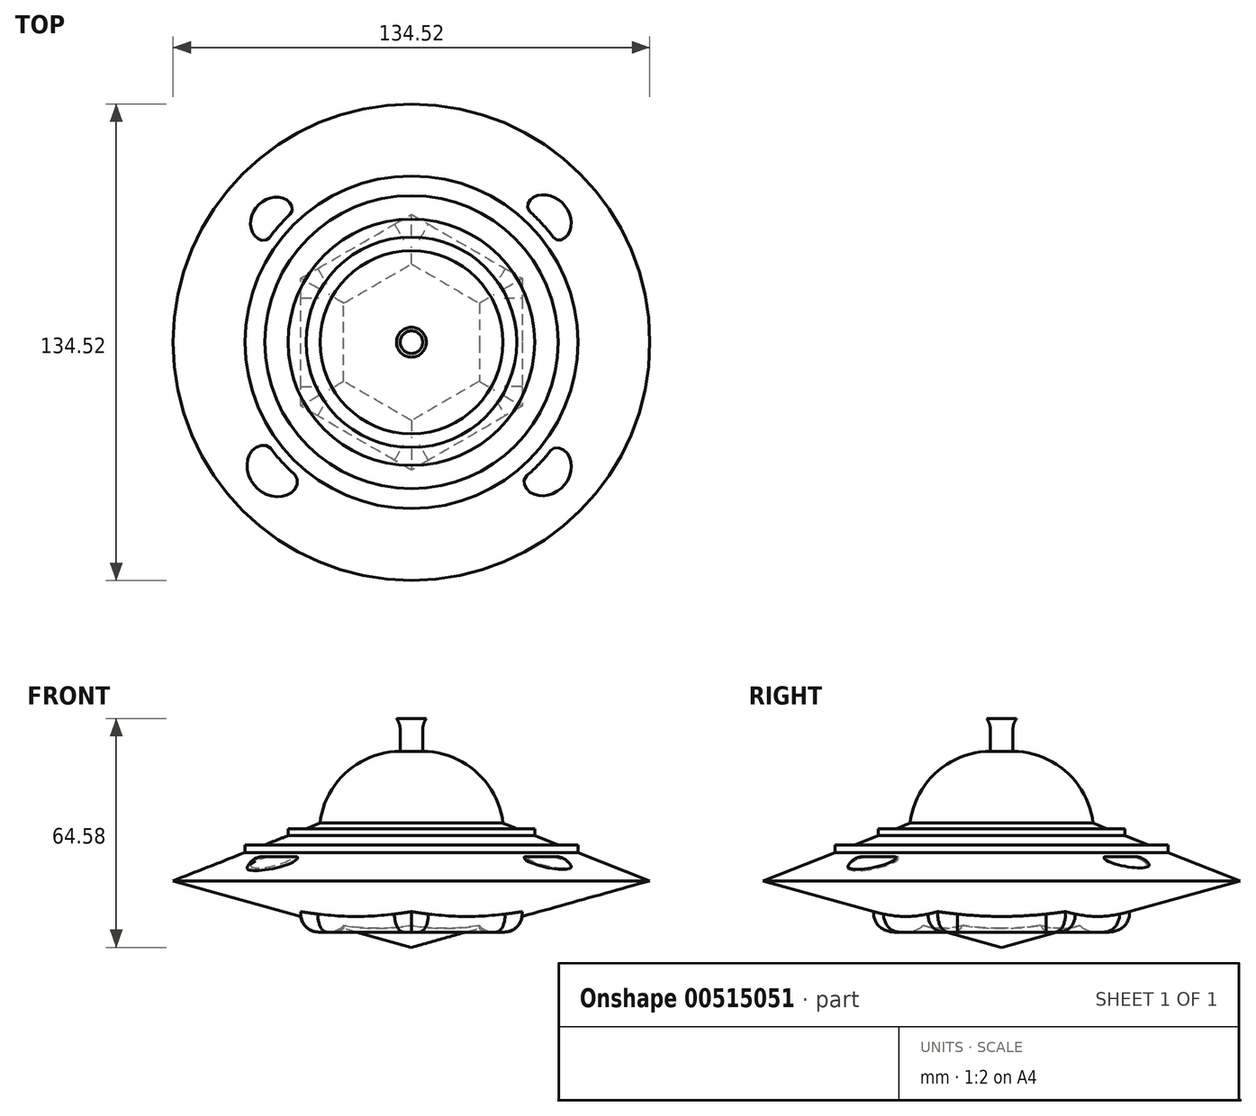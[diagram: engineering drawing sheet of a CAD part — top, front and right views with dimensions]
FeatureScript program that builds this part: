
annotation { "Feature Type Name" : "Feature", "Feature Type Description" : "" }
export const myFeature = defineFeature(function(context is Context, id is Id, definition is map)
    precondition{}
    {
        {
            var Q0;
            Q0=qCreatedBy(makeId("Front.planeOp"),FACE);
            var sketch = newSketch(context, id + "F0", { "sketchPlane" : qUnion([Q0])});
            skLineSegment(sketch, "E0", {"start": v(0, -18.8) * mm, "end": v(67.26, 0) * mm});
            skLineSegment(sketch, "E1", {"start": v(67.26, 0) * mm, "end": v(25.82, 16.26) * mm});
            skArc(sketch, "E2", {"start": v(25.82, 16.26) * mm, "mid": v(17.12, 31.7) * mm, "end": v(0, 36.34) * mm});
            skLineSegment(sketch, "E3", {"start": v(0, 36.34) * mm, "end": v(0, -18.8) * mm});
            skLineSegment(sketch, "E4", {"start": v(0, 36.34) * mm, "end": v(0, -18.8) * mm, "construction": true});
            skSolve(sketch);
        }
        {
            var Q0;
            Q0 = qSketchRegion(id + "F0", true);
            var Q1;
            Q1=sQuery(id+"F0.wireOp",EDGE,"E3");
            revolve(context, id + "F1", {"entities" : qUnion([Q0]), "axis" : qUnion([Q1]), "revolveType" : RevolveType.FULL});
        }
        {
            var Q0;
            Q0=qCreatedBy(makeId("Top.planeOp"),FACE);
            var sketch = newSketch(context, id + "F2", { "sketchPlane" : qUnion([Q0])});
            skCircle(sketch, "E5.cCircle", {"center": v(0, 0) * mm, "radius": 26.96 * mm, "construction": true});
            skLineSegment(sketch, "E5.0", {"start": v(31.13, 0.69) * mm, "end": v(16.16, -26.61) * mm});
            skLineSegment(sketch, "E5.1", {"start": v(16.16, -26.61) * mm, "end": v(-14.97, -27.3) * mm});
            skLineSegment(sketch, "E5.2", {"start": v(-14.97, -27.3) * mm, "end": v(-31.13, -0.69) * mm});
            skLineSegment(sketch, "E5.3", {"start": v(-31.13, -0.69) * mm, "end": v(-16.16, 26.61) * mm});
            skLineSegment(sketch, "E5.4", {"start": v(-16.16, 26.61) * mm, "end": v(14.97, 27.3) * mm});
            skLineSegment(sketch, "E5.5", {"start": v(14.97, 27.3) * mm, "end": v(31.13, 0.69) * mm});
            skPoint(sketch, "E5.0.midPoint", {"position": v(23.64, -12.96) * mm});
            skSolve(sketch);
        }
        {
            var Q0;
            Q0 = qSketchRegion(id + "F2", true);
            extrude(context, id + "F3", {"entities" : qUnion([Q0]), "operationType" : NewBodyOperationType.ADD, "oppositeDirection" : true, "depth" : 5.33 * mm, "offsetDistance" : 25.4 * mm});
        }
        {
            var Q0;
            Q0=qCreatedBy(makeId("Top.planeOp"),FACE);
            var sketch = newSketch(context, id + "F4", { "sketchPlane" : qUnion([Q0])});
            skCircle(sketch, "E6", {"center": v(-36.65, 32.37) * mm, "radius": 9.48 * mm});
            skCircle(sketch, "E7", {"center": v(35.69, 32.37) * mm, "radius": 10.16 * mm});
            skCircle(sketch, "E8", {"center": v(35.69, -33.96) * mm, "radius": 9.99 * mm});
            skCircle(sketch, "E9", {"center": v(-36.65, -33.96) * mm, "radius": 10.14 * mm});
            skSolve(sketch);
        }
        {
            var Q0;
            Q0 = qSketchRegion(id + "F4", true);
            extrude(context, id + "F5", {"entities" : qUnion([Q0]), "operationType" : NewBodyOperationType.ADD, "depth" : 6.86 * mm, "offsetDistance" : 25.4 * mm});
        }
        {
            var Q0;
            Q0=qCreatedBy(makeId("Front.planeOp"),FACE);
            var sketch = newSketch(context, id + "F6", { "sketchPlane" : qUnion([Q0])});
            skLineSegment(sketch, "E10", {"start": v(3.19, 35.7) * mm, "end": v(3.19, 44.95) * mm});
            skArc(sketch, "E11", {"start": v(3.19, 44.95) * mm, "mid": v(4.2, 49.02) * mm, "end": v(0, 49.09) * mm});
            skLineSegment(sketch, "E12", {"start": v(0, 49.09) * mm, "end": v(0, 34.43) * mm});
            skLineSegment(sketch, "E13", {"start": v(0, 34.43) * mm, "end": v(3.19, 35.7) * mm});
            skLineSegment(sketch, "E14", {"start": v(0, 49.09) * mm, "end": v(0, 34.43) * mm, "construction": true});
            skSolve(sketch);
        }
        {
            var Q0;
            Q0 = qSketchRegion(id + "F6", true);
            var Q1;
            Q1=sQuery(id+"F6.wireOp",EDGE,"E12");
            revolve(context, id + "F7", {"operationType" : NewBodyOperationType.ADD, "entities" : qUnion([Q0]), "axis" : qUnion([Q1]), "revolveType" : RevolveType.FULL});
        }
        {
            var Q0;
            Q0=makeQuery(id+"F5.opExtrude","CAP_EDGE",EDGE,{"disambiguationData":[OSD([sQuery(id+"F4.wireOp",EDGE,"E8")])],"isStart":false});
            var Q1;
            Q1=makeQuery(id+"F5.opExtrude","CAP_EDGE",EDGE,{"disambiguationData":[OSD([sQuery(id+"F4.wireOp",EDGE,"E7")])],"isStart":false});
            var Q2;
            Q2=makeQuery(id+"F5.opExtrude","CAP_EDGE",EDGE,{"disambiguationData":[OSD([sQuery(id+"F4.wireOp",EDGE,"E6")])],"isStart":false});
            var Q3;
            Q3=makeQuery(id+"F5.opExtrude","CAP_EDGE",EDGE,{"disambiguationData":[OSD([sQuery(id+"F4.wireOp",EDGE,"E9")])],"isStart":false});
            var Q4;
            Q4=makeQuery(id+"F7.opRevolve","SWEPT_FACE",FACE,{"disambiguationData":[OSD([sQuery(id+"F6.wireOp",EDGE,"E11")])]});
            fillet(context, id + "F8", {"entities" : qUnion([Q0, Q1, Q2, Q3, Q4]), "radius" : 5.08 * mm, "tangentPropagation" : true, "allowEdgeOverflow" : false});
        }
        {
            var Q0;
            Q0=qCreatedBy(makeId("Top.planeOp"),FACE);
            var sketch = newSketch(context, id + "F9", { "sketchPlane" : qUnion([Q0])});
            skCircle(sketch, "E15", {"center": v(0, 0) * mm, "radius": 46.94 * mm});
            skSolve(sketch);
        }
        {
            var Q0;
            Q0 = qSketchRegion(id + "F9", true);
            extrude(context, id + "F10", {"entities" : qUnion([Q0]), "operationType" : NewBodyOperationType.ADD, "depth" : 10.16 * mm, "offsetDistance" : 25.4 * mm});
        }
        {
            var Q0;
            Q0=qCreatedBy(makeId("Top.planeOp"),FACE);
            var sketch = newSketch(context, id + "F11", { "sketchPlane" : qUnion([Q0])});
            skCircle(sketch, "E16", {"center": v(0, 0) * mm, "radius": 34.78 * mm});
            skSolve(sketch);
        }
        {
            var Q0;
            Q0 = qSketchRegion(id + "F11", true);
            extrude(context, id + "F12", {"entities" : qUnion([Q0]), "operationType" : NewBodyOperationType.ADD, "depth" : 14.73 * mm, "offsetDistance" : 25.4 * mm});
        }
        {
            var Q0;
            Q0=qCreatedBy(makeId("Top.planeOp"),FACE);
            var sketch = newSketch(context, id + "F13", { "sketchPlane" : qUnion([Q0])});
            skCircle(sketch, "E17.cCircle", {"center": v(0, 0) * mm, "radius": 31.24 * mm, "construction": true});
            skLineSegment(sketch, "E17.0", {"start": v(-31.24, -18.04) * mm, "end": v(-31.24, 18.04) * mm});
            skLineSegment(sketch, "E17.1", {"start": v(-31.24, 18.04) * mm, "end": v(0, 36.07) * mm});
            skLineSegment(sketch, "E17.2", {"start": v(0, 36.07) * mm, "end": v(31.24, 18.04) * mm});
            skLineSegment(sketch, "E17.3", {"start": v(31.24, 18.04) * mm, "end": v(31.24, -18.04) * mm});
            skLineSegment(sketch, "E17.4", {"start": v(31.24, -18.04) * mm, "end": v(0, -36.07) * mm});
            skLineSegment(sketch, "E17.5", {"start": v(0, -36.07) * mm, "end": v(-31.24, -18.04) * mm});
            skPoint(sketch, "E17.0.midPoint", {"position": v(-31.24, 0) * mm});
            skCircle(sketch, "E18.cCircle", {"center": v(0, 0) * mm, "radius": 19.14 * mm, "construction": true});
            skLineSegment(sketch, "E18.0", {"start": v(0, -22.1) * mm, "end": v(-19.13, -11.05) * mm});
            skLineSegment(sketch, "E18.1", {"start": v(-19.13, -11.05) * mm, "end": v(-19.14, 11.04) * mm});
            skLineSegment(sketch, "E18.2", {"start": v(-19.14, 11.04) * mm, "end": v(0, 22.1) * mm});
            skLineSegment(sketch, "E18.3", {"start": v(0, 22.1) * mm, "end": v(19.13, 11.05) * mm});
            skLineSegment(sketch, "E18.4", {"start": v(19.13, 11.05) * mm, "end": v(19.14, -11.04) * mm});
            skLineSegment(sketch, "E18.5", {"start": v(19.14, -11.04) * mm, "end": v(0, -22.1) * mm});
            skPoint(sketch, "E18.0.midPoint", {"position": v(-9.56, -16.58) * mm});
            skSolve(sketch);
        }
        {
            var Q0;
            Q0 = qSketchRegion(id + "F13", true);
            extrude(context, id + "F14", {"entities" : qUnion([Q0]), "operationType" : NewBodyOperationType.ADD, "oppositeDirection" : true, "depth" : 14.48 * mm, "offsetDistance" : 25.4 * mm});
        }
        {
            var Q0;
            Q0=makeQuery(id+"F14.opExtrude","CAP_FACE",FACE,{"disambiguationData":[OSD([sQuery(id+"F13.wireOp",EDGE,"E17.0"),sQuery(id+"F13.wireOp",EDGE,"E17.1"),sQuery(id+"F13.wireOp",EDGE,"E17.2"),sQuery(id+"F13.wireOp",EDGE,"E17.3"),sQuery(id+"F13.wireOp",EDGE,"E17.4"),sQuery(id+"F13.wireOp",EDGE,"E17.5"),sQuery(id+"F13.wireOp",EDGE,"E18.0"),sQuery(id+"F13.wireOp",EDGE,"E18.1"),sQuery(id+"F13.wireOp",EDGE,"E18.2"),sQuery(id+"F13.wireOp",EDGE,"E18.3"),sQuery(id+"F13.wireOp",EDGE,"E18.4"),sQuery(id+"F13.wireOp",EDGE,"E18.5")])],"isStart":false});
            fillet(context, id + "F15", {"entities" : qUnion([Q0]), "radius" : 5.08 * mm, "tangentPropagation" : true, "allowEdgeOverflow" : false});
        }
    });
